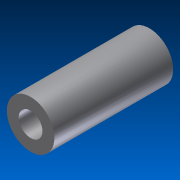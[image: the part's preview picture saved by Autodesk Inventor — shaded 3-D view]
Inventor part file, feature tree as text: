
AUTODESK INVENTOR PART (.ipt)
format: ipt  version: 2012 (Build 160160000, 160)  size: 80,384 bytes
history: native  units: in
note: dims shown in document units (in); Inventor stores cm internally (conversion verified against a paired STEP export)
features: extrude x1, sketch x1
ambient origin geometry x8: Origin, YZ Plane, XZ Plane, XY Plane, X Axis, Y Axis, Z Axis, Center Point
bodies: Solid1 (feature_tree)
feature tree (2):
  extrude  "Extrusion1"  Depth=0.2362in
  sketch  "Sketch1"  dims[d0=0.1181in d1=0.2362in d2=0.5906in d3=0.0in]
